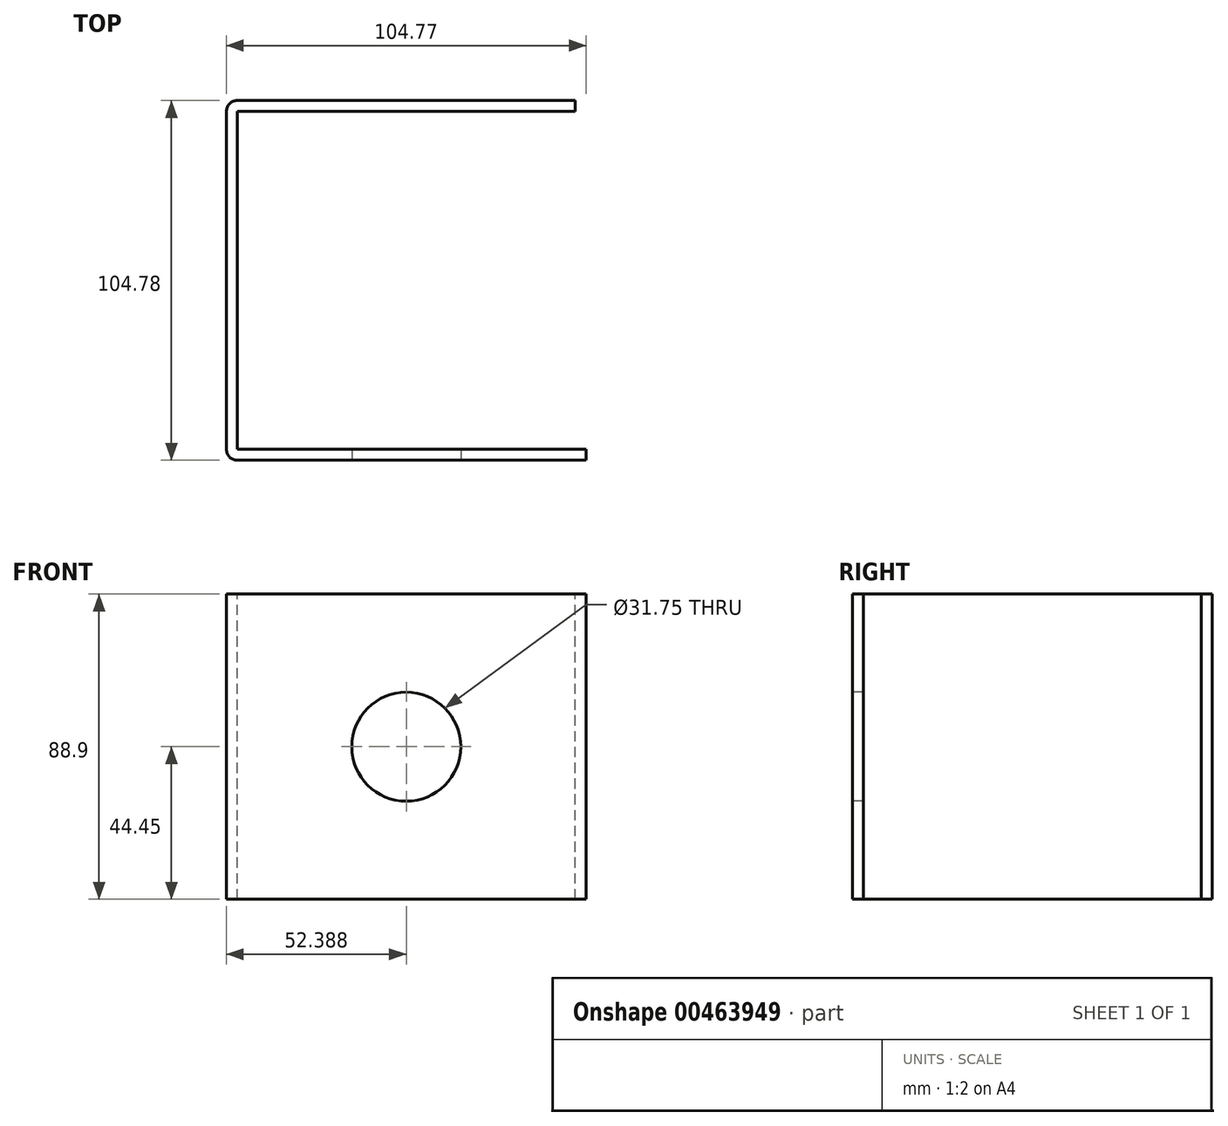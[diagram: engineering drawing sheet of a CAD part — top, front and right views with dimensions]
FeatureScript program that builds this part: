
annotation { "Feature Type Name" : "Feature", "Feature Type Description" : "" }
export const myFeature = defineFeature(function(context is Context, id is Id, definition is map)
    precondition{}
    {
        {
            var Q0;
            Q0=qCreatedBy(makeId("Front.planeOp"),FACE);
            var sketch = newSketch(context, id + "F0", { "sketchPlane" : qUnion([Q0])});
            skLineSegment(sketch, "E0.bottom", {"start": v(0, 0) * mm, "end": v(101.6, 0) * mm});
            skLineSegment(sketch, "E0.top", {"start": v(0, 88.9) * mm, "end": v(101.6, 88.9) * mm});
            skLineSegment(sketch, "E0.left", {"start": v(0, 0) * mm, "end": v(0, 88.9) * mm});
            skLineSegment(sketch, "E0.right", {"start": v(101.6, 0) * mm, "end": v(101.6, 88.9) * mm});
            skSolve(sketch);
        }
        {
            var Q0;
            Q0=qSketchRegion(id+"F0",true);
            extrude(context, id + "F1", {"entities" : qUnion([Q0]), "depth" : 3.17 * mm});
        }
        {
            var Q0;
            Q0=makeQuery(id+"F1.opExtrude","CAP_FACE",FACE,{"disambiguationData":[OSD([sQuery(id+"F0.wireOp",EDGE,"E0.bottom"),sQuery(id+"F0.wireOp",EDGE,"E0.top"),sQuery(id+"F0.wireOp",EDGE,"E0.left"),sQuery(id+"F0.wireOp",EDGE,"E0.right")])],"isStart":false});
            var sketch = newSketch(context, id + "F2", { "sketchPlane" : qUnion([Q0])});
            skLineSegment(sketch, "E1.bottom", {"start": v(0, 0) * mm, "end": v(3.18, 0) * mm});
            skLineSegment(sketch, "E1.top", {"start": v(0, 88.9) * mm, "end": v(3.17, 88.9) * mm});
            skLineSegment(sketch, "E1.left", {"start": v(0, 0) * mm, "end": v(0, 88.9) * mm});
            skLineSegment(sketch, "E1.right", {"start": v(3.18, 0) * mm, "end": v(3.17, 88.9) * mm});
            skSolve(sketch);
        }
        {
            var Q0;
            Q0=qSketchRegion(id+"F2",true);
            extrude(context, id + "F3", {"entities" : qUnion([Q0]), "operationType" : NewBodyOperationType.ADD, "depth" : 101.6 * mm});
        }
        {
            var Q0;
            Q0=makeQuery(id+"F3.opExtrude","SWEPT_FACE",FACE,{"disambiguationData":[OSD([sQuery(id+"F2.wireOp",EDGE,"E1.right")])]});
            var sketch = newSketch(context, id + "F4", { "sketchPlane" : qUnion([Q0])});
            skLineSegment(sketch, "E2.bottom", {"start": v(-104.78, 88.9) * mm, "end": v(-101.6, 88.9) * mm});
            skLineSegment(sketch, "E2.top", {"start": v(-104.78, 0) * mm, "end": v(-101.6, 0) * mm});
            skLineSegment(sketch, "E2.left", {"start": v(-104.78, 88.9) * mm, "end": v(-104.78, 0) * mm});
            skLineSegment(sketch, "E2.right", {"start": v(-101.6, 88.9) * mm, "end": v(-101.6, 0) * mm});
            skSolve(sketch);
        }
        {
            var Q0;
            Q0=qSketchRegion(id+"F4",true);
            extrude(context, id + "F5", {"entities" : qUnion([Q0]), "operationType" : NewBodyOperationType.ADD, "depth" : 101.6 * mm});
        }
        {
            var Q0;
            Q0=makeQuery(id+"F5.boolean.opBoolean","MERGE",FACE,{"derivedFrom":[makeQuery(id+"F3.opExtrude","CAP_FACE",FACE,{"disambiguationData":[OSD([sQuery(id+"F2.wireOp",EDGE,"E1.bottom"),sQuery(id+"F2.wireOp",EDGE,"E1.top"),sQuery(id+"F2.wireOp",EDGE,"E1.left"),sQuery(id+"F2.wireOp",EDGE,"E1.right")])],"isStart":false}),makeQuery(id+"F5.opExtrude","SWEPT_FACE",FACE,{"disambiguationData":[OSD([sQuery(id+"F4.wireOp",EDGE,"E2.left")])]})]});
            var sketch = newSketch(context, id + "F6", { "sketchPlane" : qUnion([Q0])});
            skCircle(sketch, "E3", {"center": v(52.39, 44.45) * mm, "radius": 15.88 * mm});
            skLineSegment(sketch, "E4", {"start": v(0, 44.45) * mm, "end": v(104.78, 44.45) * mm});
            skSolve(sketch);
        }
        {
            var Q0;
            Q0 = qSketchRegion(id + "F6", true);
            extrude(context, id + "F7", {"entities" : qUnion([Q0]), "operationType" : NewBodyOperationType.REMOVE, "endBound" : BoundingType.UP_TO_NEXT, "oppositeDirection" : true, "depth" : 25.4 * mm});
        }
        {
            var Q0;
            Q0=makeQuery(id+"F3.opExtrude","CAP_EDGE",EDGE,{"disambiguationData":[OSD([sQuery(id+"F2.wireOp",EDGE,"E1.left")])],"isStart":false});
            var Q1;
            Q1=makeQuery(id+"F1.opExtrude","CAP_EDGE",EDGE,{"disambiguationData":[OSD([sQuery(id+"F0.wireOp",EDGE,"E0.left")])],"isStart":true});
            fillet(context, id + "F8", {"entities" : qUnion([Q0, Q1]), "radius" : 3.17 * mm, "tangentPropagation" : true, "allowEdgeOverflow" : false});
        }
    });
